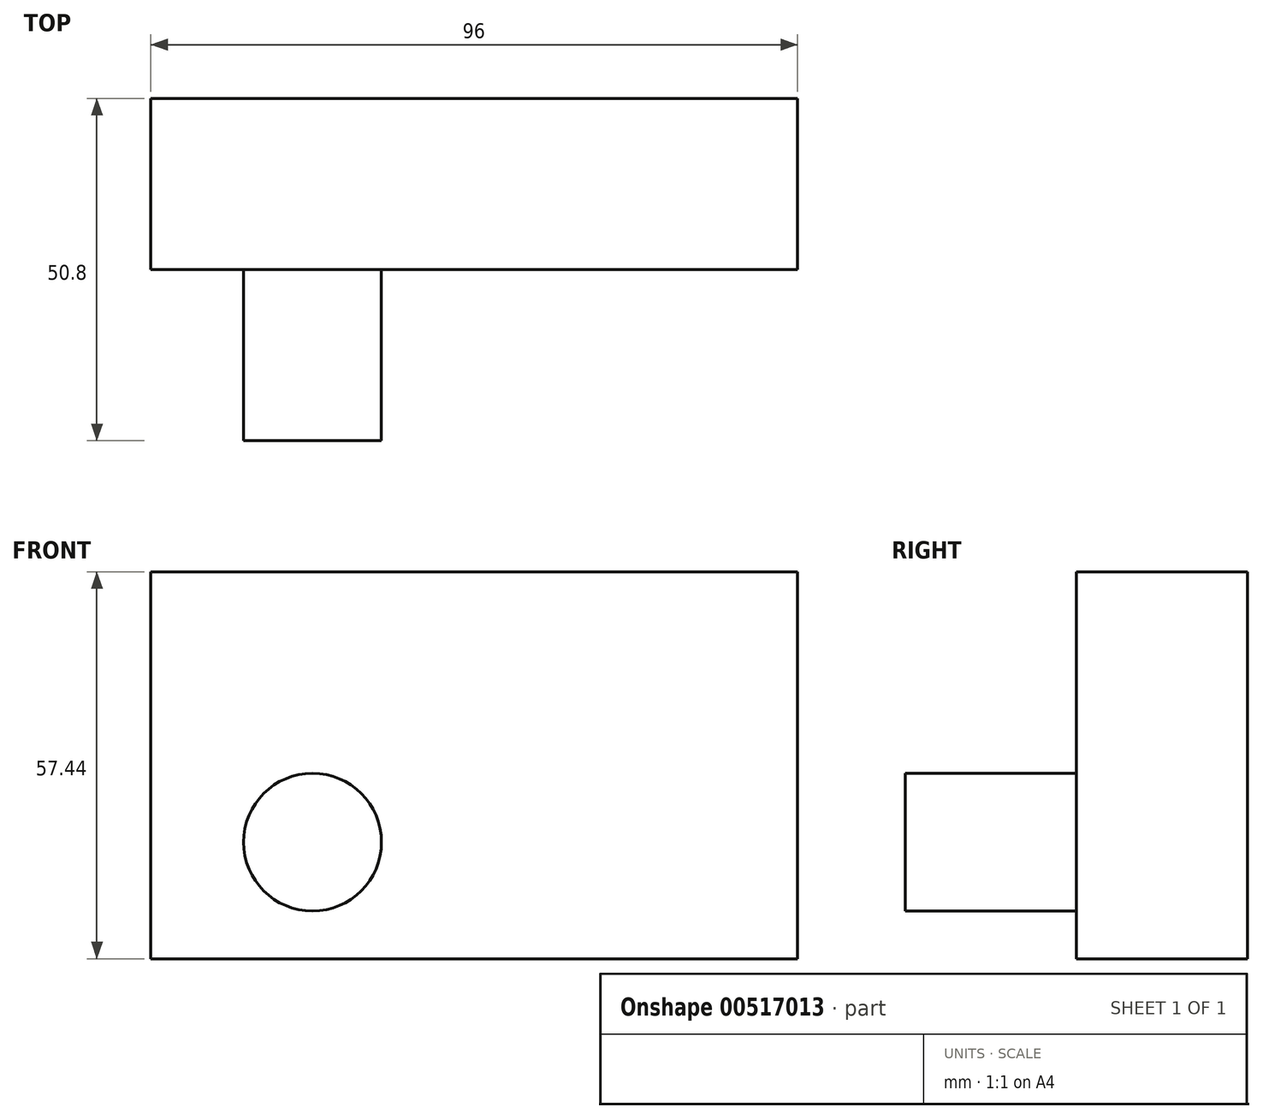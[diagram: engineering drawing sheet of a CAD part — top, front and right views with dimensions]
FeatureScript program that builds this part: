
annotation { "Feature Type Name" : "Feature", "Feature Type Description" : "" }
export const myFeature = defineFeature(function(context is Context, id is Id, definition is map)
    precondition{}
    {
        {
            var Q0;
            Q0=qCreatedBy(makeId("Front.planeOp"),FACE);
            var sketch = newSketch(context, id + "F0", { "sketchPlane" : qUnion([Q0])});
            skLineSegment(sketch, "E0.bottom", {"start": v(-48, 28.72) * mm, "end": v(48, 28.72) * mm});
            skLineSegment(sketch, "E0.top", {"start": v(-48, -28.72) * mm, "end": v(48, -28.72) * mm});
            skLineSegment(sketch, "E0.left", {"start": v(-48, 28.72) * mm, "end": v(-48, -28.72) * mm});
            skLineSegment(sketch, "E0.right", {"start": v(48, 28.72) * mm, "end": v(48, -28.72) * mm});
            skPoint(sketch, "E0.middle", {"position": v(0, 0) * mm});
            skSolve(sketch);
        }
        {
            var Q0;
            Q0=makeQuery(id+"F0.imprint","IMPRINT",FACE,{"disambiguationData":[TD([[makeQuery(id+"F0.imprint","IMPRINT",EDGE,{"derivedFrom":sQuery(id+"F0.wireOp",EDGE,"E0.bottom")}),-1.0]])]});
            extrude(context, id + "F1", {"entities" : qUnion([Q0]), "endBound" : BoundingType.SYMMETRIC, "depth" : 25.4 * mm, "offsetDistance" : 25.4 * mm});
        }
        {
            var Q0;
            Q0=makeQuery(id+"F1.opExtrude","CAP_FACE",FACE,{"disambiguationData":[OSD([sQuery(id+"F0.wireOp",EDGE,"E0.bottom"),sQuery(id+"F0.wireOp",EDGE,"E0.top"),sQuery(id+"F0.wireOp",EDGE,"E0.left"),sQuery(id+"F0.wireOp",EDGE,"E0.right")])],"isStart":false});
            var sketch = newSketch(context, id + "F2", { "sketchPlane" : qUnion([Q0])});
            skCircle(sketch, "E1", {"center": v(-24, -11.41) * mm, "radius": 10.23 * mm});
            skSolve(sketch);
        }
        {
            var Q0;
            Q0=makeQuery(id+"F2.imprint","IMPRINT",FACE,{"disambiguationData":[TD([[makeQuery(id+"F2.imprint","IMPRINT",EDGE,{"derivedFrom":sQuery(id+"F2.wireOp",EDGE,"E1")}),1.0]])]});
            extrude(context, id + "F3", {"entities" : qUnion([Q0]), "operationType" : NewBodyOperationType.ADD, "depth" : 25.4 * mm, "offsetDistance" : 25.4 * mm});
        }
    });
